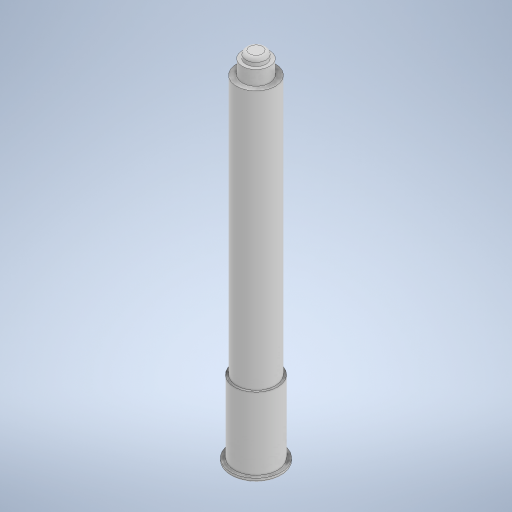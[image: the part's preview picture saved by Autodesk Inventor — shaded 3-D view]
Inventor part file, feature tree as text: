
AUTODESK INVENTOR PART (.ipt)
format: ipt  version: 2023 (Build 270158030, 158C)  size: 267,776 bytes
history: native  units: in
note: dims shown in document units (in); Inventor stores cm internally (conversion verified against a paired STEP export)
features: extrude x5, sketch x5, fillet x2
ambient origin geometry x8: Origin, YZ Plane, XZ Plane, XY Plane, X Axis, Y Axis, Z Axis, Center Point
bodies: Solid1 (feature_tree)
feature tree (12):
  extrude  "Extrusion1"  Depth=0.125in TaperAngle=0.0deg
  fillet  "Fillet1"  Radius=0.05in
  extrude  "Extrusion2"  Depth=2.5in TaperAngle=0.0deg
  extrude  "Extrusion3"  Depth=9.0in TaperAngle=0.0deg
  extrude  "Extrusion4"  Depth=0.5in TaperAngle=0.0deg
  extrude  "Extrusion5"  Depth=0.25in TaperAngle=0.0deg
  fillet  "Fillet3"  Radius=0.125in
  sketch  "Sketch1"  dims[d0=1.75in d1=0.125in d2=0.0in d3=0.05in]
  sketch  "Sketch2"  dims[d4=1.5in d5=2.5in d6=0.0in]
  sketch  "Sketch3"  dims[d7=1.35in d8=9.0in d9=0.0in]
  sketch  "Sketch4"  dims[d10=0.95in d11=0.5in d12=0.0in]
  sketch  "Sketch5"  dims[d14=0.7in d15=0.25in d16=0.0in d17=0.125in]
